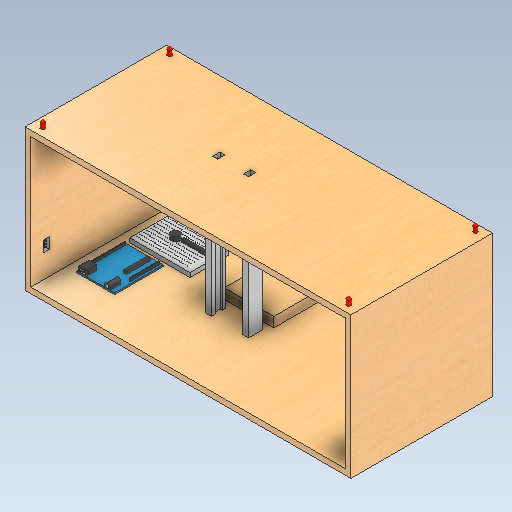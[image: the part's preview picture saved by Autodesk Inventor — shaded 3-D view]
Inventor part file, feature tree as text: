
AUTODESK INVENTOR PART (.ipt)
format: ipt  version: 2021 (Build 250183000, 183)  size: 986,624 bytes
history: native  units: mm
features: extrude x21, sketch x21, fillet x2, pattern_linear x2, hole x1
ambient origin geometry x8: Origin, YZ Plane, XZ Plane, XY Plane, X Axis, Y Axis, Z Axis, Center Point
bodies: Solid1 (feature_tree)
feature tree (47):
  extrude  "Extrusion1"  Depth=200.0mm
  extrude  "Extrusion2"  Depth=200.0mm TaperAngle=0.0deg
  extrude  "Extrusion4"  Depth=75.0mm
  extrude  "Extrusion5"  Depth=7.0mm
  extrude  "Extrusion6"  Depth=241.14mm
  extrude  "Extrusion7"  Depth=7.0mm
  extrude  "Extrusion8"  Depth=100.0mm TaperAngle=0.0deg
  fillet  "Fillet1"  Radius=3.0mm
  extrude  "Extrusion9"  Depth=3.0mm
  extrude  "Extrusion10"  Depth=96.68mm
  extrude  "Extrusion11"  Depth=190.0mm TaperAngle=0.0deg
  extrude  "Extrusion12"  Depth=10.0mm
  extrude  "Extrusion13"  Depth=50.35mm
  extrude  "Extrusion14"  Depth=53.4mm
  hole  "Hole1"  [1 undecoded]
  pattern_linear  "Rectangular Pattern1"  Count1=5  [1 undecoded]
  pattern_linear  "Rectangular Pattern2"  Spacing1=4.0mm  [1 undecoded]
  extrude  "Extrusion15"  Depth=4.0mm TaperAngle=0.0deg
  extrude  "Extrusion16"  Depth=3.0mm TaperAngle=0.0deg
  extrude  "Extrusion17"  Depth=7.0mm TaperAngle=0.0deg
  extrude  "Extrusion18"  Depth=8.0mm
  extrude  "Extrusion19"  Depth=3.0mm
  extrude  "Extrusion20"  Depth=85.0mm
  extrude  "Extrusion21"  Depth=55.0mm
  extrude  "Extrusion22"  Depth=6.0mm TaperAngle=0.0deg
  fillet  "Fillet2"  Radius=3.0mm
  sketch  "Sketch1"  dims[d0=460.0mm d1=200.0mm]
  sketch  "Sketch4"  dims[d2=8.0mm d3=200.0mm d4=0.0mm]
  sketch  "Sketch5"  dims[d5=70.0mm d6=75.0mm]
  sketch  "Sketch6"  dims[d9=14.0mm d10=0.0mm d16=7.0mm]
  sketch  "Sketch7"  dims[d17=10.0mm d18=241.14mm]
  sketch  "Sketch8"  dims[d19=93.32mm d20=7.0mm d21=10.0mm d22=93.32mm]
  sketch  "Sketch9"  dims[d23=36.35mm d24=100.0mm d25=0.0mm d26=3.0mm]
  sketch  "Sketch10"  dims[d27=10.0mm d28=3.0mm]
  sketch  "Sketch11"  dims[d29=5.0mm d30=96.68mm]
  sketch  "Sketch12"  dims[d31=168.51mm d32=190.0mm d33=0.0mm]
  sketch  "Sketch13"  dims[d34=3.0mm d35=10.0mm]
  sketch  "Sketch14"  dims[d36=5.0mm d37=50.35mm]
  sketch  "Sketch15"  dims[d38=96.68mm d39=53.4mm]
  sketch  "Sketch16"  dims[d40=68.6mm d41=15.0mm d42=50.0mm]
  sketch  "Sketch17"  dims[d43=2.0mm d44=0.0mm]
  sketch  "Sketch18"  dims[d45=1.0mm]
  sketch  "Sketch19"  dims[d46=1.0mm]
  sketch  "Sketch21"  dims[d47=4.0mm d48=0.0mm]
  sketch  "Sketch22"  dims[d49=7.0mm d50=0.0mm]
  sketch  "Sketch23"  dims[d51=3.83mm]
  sketch  "Sketch24"  dims[d52=3.0mm d53=0.0mm d54=4.0mm d55=0.0mm d56=4.0mm d57=0.0mm d58=3.0mm d59=0.0mm d60=7.0mm d61=0.0mm d62=8.0mm d63=3.0mm d64=85.0mm d65=55.0mm d66=6.0mm d67=0.0mm d68=1.0mm d69=6.0mm d70=4.0mm d71=2.0mm d72=90.0deg d73=3.0mm d74=0.0mm d75=250.0mm d77=3.0mm d78=100.0mm d80=5.0mm d81=6.0mm d82=0.0mm d83=1.0mm d84=0.0mm d85=3.0mm d86=0.0mm d87=90.0mm d89=3.0mm d90=10.0mm d92=10.0mm d94=0.7mm d95=0.0mm d96=90.0mm d98=3.0mm d99=10.0mm d101=10.0mm d103=0.7mm d104=0.0mm d105=10.0mm d106=0.0mm d107=30.0mm d109=4.0mm d110=10.0mm d112=10.0mm d114=7.0mm d115=0.0mm d116=6.0mm d117=10.0mm d118=0.0mm d119=3.0mm d120=14.0mm d121=10.0mm d122=20.0mm d124=432.0mm d125=10.0mm d127=10.0mm d129=20.0mm d131=179.0mm d132=10.0mm d134=10.0mm]
note: 3 required parameter values undecoded (feature->parameter linkage not recoverable at this tier; creation-order binding heuristic only, values carry confidence <= 0.55)
